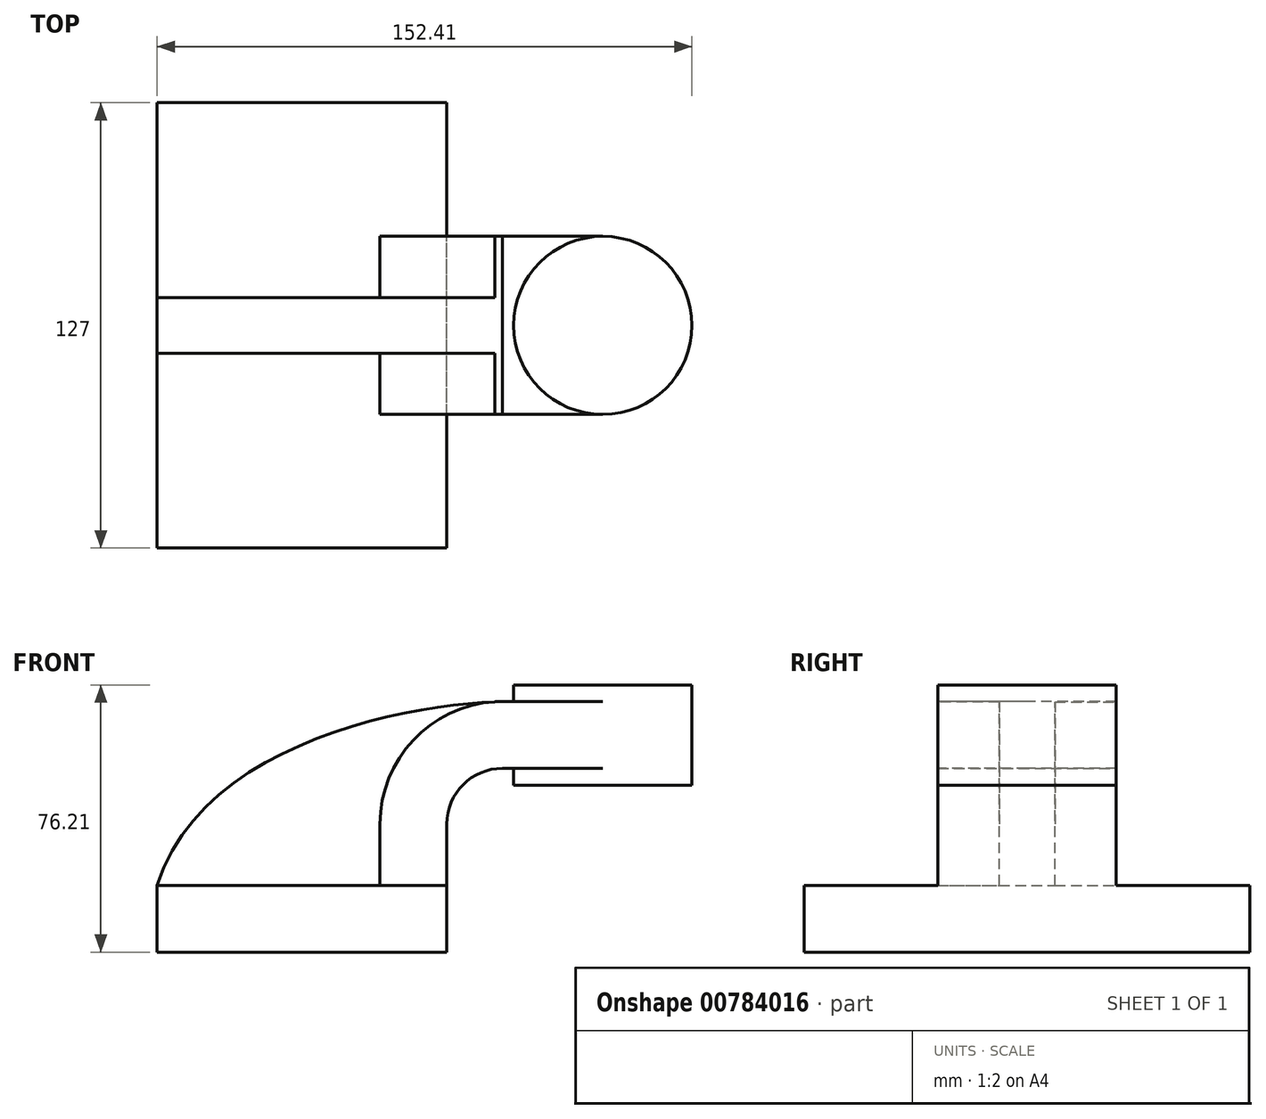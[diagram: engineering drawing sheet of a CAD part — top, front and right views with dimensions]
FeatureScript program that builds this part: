
annotation { "Feature Type Name" : "Feature", "Feature Type Description" : "" }
export const myFeature = defineFeature(function(context is Context, id is Id, definition is map)
    precondition{}
    {
        {
            var Q0;
            Q0=qCreatedBy(makeId("Front.planeOp"),FACE);
            var sketch = newSketch(context, id + "F0", { "sketchPlane" : qUnion([Q0])});
            skLineSegment(sketch, "E0.bottom", {"start": v(41.28, -9.52) * mm, "end": v(-41.28, -9.52) * mm});
            skLineSegment(sketch, "E0.top", {"start": v(41.28, 9.53) * mm, "end": v(-41.28, 9.53) * mm});
            skLineSegment(sketch, "E0.left", {"start": v(41.28, -9.52) * mm, "end": v(41.28, 9.53) * mm});
            skLineSegment(sketch, "E0.right", {"start": v(-41.28, -9.52) * mm, "end": v(-41.28, 9.53) * mm});
            skPoint(sketch, "E0.middle", {"position": v(0, 0) * mm});
            skLineSegment(sketch, "E1.bottom", {"start": v(60.32, 38.1) * mm, "end": v(111.13, 38.1) * mm});
            skLineSegment(sketch, "E1.top", {"start": v(60.32, 66.68) * mm, "end": v(111.12, 66.68) * mm});
            skLineSegment(sketch, "E1.left", {"start": v(60.32, 38.1) * mm, "end": v(60.32, 66.68) * mm});
            skLineSegment(sketch, "E1.right", {"start": v(111.13, 38.1) * mm, "end": v(111.12, 66.68) * mm});
            skPoint(sketch, "E1.middle", {"position": v(85.72, 52.39) * mm});
            skLineSegment(sketch, "E2", {"start": v(41.28, 9.53) * mm, "end": v(41.28, 27) * mm});
            skArc(sketch, "E3", {"start": v(41.27, 27) * mm, "mid": v(45.92, 38.23) * mm, "end": v(57.15, 42.88) * mm});
            skLineSegment(sketch, "E4", {"start": v(57.15, 42.88) * mm, "end": v(85.72, 42.88) * mm});
            skLineSegment(sketch, "E5.0", {"start": v(57.15, 61.93) * mm, "end": v(92.25, 61.93) * mm});
            skArc(sketch, "E5.1", {"start": v(22.23, 27) * mm, "mid": v(32.45, 51.7) * mm, "end": v(57.15, 61.93) * mm});
            skLineSegment(sketch, "E5.2", {"start": v(22.22, 9.53) * mm, "end": v(22.22, 27) * mm});
            skLineSegment(sketch, "E6", {"start": v(85.72, 38.1) * mm, "end": v(85.72, 66.68) * mm});
            skFitSpline(sketch, "E7", {"points": [v(-41.28, 9.52) * mm, v(57.15, 61.93) * mm], "startDerivative": vector(39.59, 123.97) * mm, "endDerivative": vector(76.92, 1.68) * mm});
            skSolve(sketch);
        }
        {
            var Q0;
            Q0=makeQuery(id+"F0.imprint","IMPRINT",FACE,{"disambiguationData":[TD([[makeQuery(id+"F0.imprint","IMPRINT",EDGE,{"derivedFrom":sQuery(id+"F0.wireOp",EDGE,"E0.bottom")}),-1.0]])]});
            extrude(context, id + "F1", {"entities" : qUnion([Q0]), "endBound" : BoundingType.SYMMETRIC, "depth" : 127 * mm, "offsetDistance" : 25.4 * mm});
        }
        {
            var Q0;
            {var subQ0=sQuery(id+"F0.wireOp",EDGE,"E4");var subQ1=sQuery(id+"F0.wireOp",EDGE,"E1.left");var subQ2=makeQuery(id+"F0.imprint","INTERSECT",VERTEX,{"derivedFrom":[subQ1,subQ0]});Q0=makeQuery(id+"F0.imprint","IMPRINT",FACE,{"disambiguationData":[TD([[makeQuery(id+"F0.imprint","IMPRINT",EDGE,{"disambiguationData":[TD([[subQ2,-1.0]])],"derivedFrom":subQ1}),-1.0]])]});}
            var Q1;
            {var subQ1=sQuery(id+"F0.wireOp",EDGE,"E2");Q1=makeQuery(id+"F0.imprint","IMPRINT",FACE,{"disambiguationData":[TD([[makeQuery(id+"F0.imprint","IMPRINT",EDGE,{"derivedFrom":subQ1}),1.0]])]});}
            extrude(context, id + "F2", {"entities" : qUnion([Q0, Q1]), "operationType" : NewBodyOperationType.ADD, "endBound" : BoundingType.SYMMETRIC, "depth" : 50.8 * mm, "offsetDistance" : 25.4 * mm});
        }
        {
            var Q0;
            {var subQ3=sQuery(id+"F0.wireOp",EDGE,"E5.2");Q0=makeQuery(id+"F0.imprint","IMPRINT",FACE,{"disambiguationData":[TD([[makeQuery(id+"F0.imprint","IMPRINT",EDGE,{"derivedFrom":subQ3}),1.0]])]});}
            extrude(context, id + "F3", {"entities" : qUnion([Q0]), "operationType" : NewBodyOperationType.ADD, "endBound" : BoundingType.SYMMETRIC, "depth" : 15.88 * mm, "offsetDistance" : 25.4 * mm});
        }
        {
            var Q0;
            {var subQ4=sQuery(id+"F0.wireOp",EDGE,"E1.right");Q0=makeQuery(id+"F0.imprint","IMPRINT",FACE,{"disambiguationData":[TD([[makeQuery(id+"F0.imprint","IMPRINT",EDGE,{"derivedFrom":subQ4}),1.0]])]});}
            var Q1;
            Q1=sQuery(id+"F0.wireOp",EDGE,"E6");
            revolve(context, id + "F4", {"operationType" : NewBodyOperationType.ADD, "surfaceOperationType" : NewSurfaceOperationType.NEW, "entities" : qUnion([Q0]), "axis" : qUnion([Q1]), "revolveType" : RevolveType.FULL});
        }
    });
